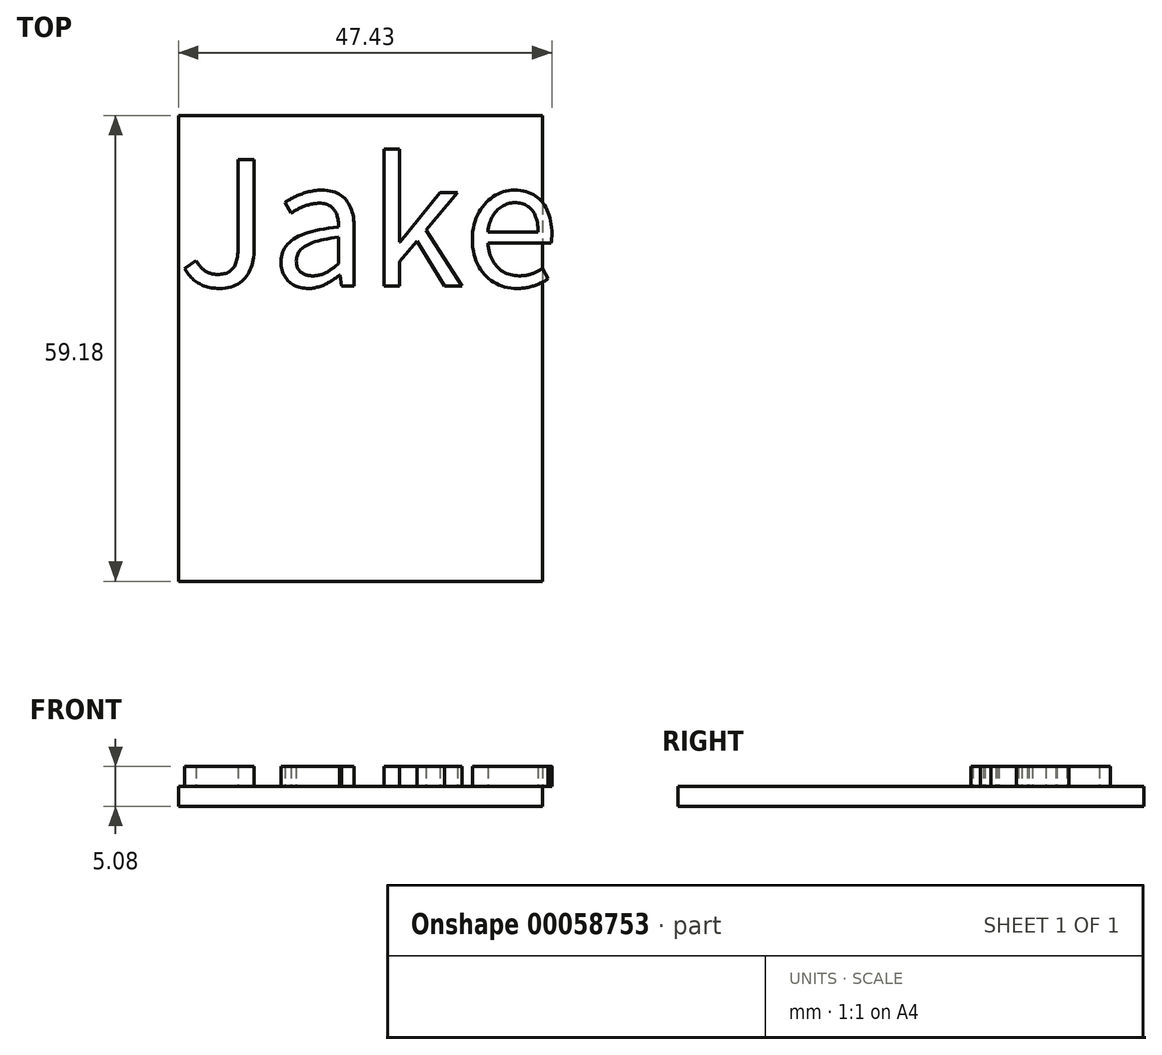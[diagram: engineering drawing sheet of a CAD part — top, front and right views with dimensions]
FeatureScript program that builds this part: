
annotation { "Feature Type Name" : "Feature", "Feature Type Description" : "" }
export const myFeature = defineFeature(function(context is Context, id is Id, definition is map)
    precondition{}
    {
        {
            var Q0;
            Q0=qCreatedBy(makeId("Top.planeOp"),FACE);
            var sketch = newSketch(context, id + "F0", { "sketchPlane" : qUnion([Q0])});
            skLineSegment(sketch, "E0", {"start": v(0, 0) * mm, "end": v(0, 59.18) * mm});
            skLineSegment(sketch, "E1", {"start": v(0, 59.18) * mm, "end": v(46.24, 59.18) * mm});
            skLineSegment(sketch, "E2", {"start": v(46.24, 59.18) * mm, "end": v(46.24, 0) * mm});
            skLineSegment(sketch, "E3", {"start": v(46.24, 0) * mm, "end": v(0, 0) * mm});
            skSolve(sketch);
        }
        {
            var Q0;
            Q0=makeQuery(id+"F0.imprint","IMPRINT",FACE,{"disambiguationData":[TD([[makeQuery(id+"F0.imprint","IMPRINT",EDGE,{"derivedFrom":sQuery(id+"F0.wireOp",EDGE,"E0")}),-1.0]])]});
            extrude(context, id + "F1", {"entities" : qUnion([Q0]), "depth" : 2.54 * mm});
        }
        {
            var Q0;
            Q0=makeQuery(id+"F1.opExtrude","CAP_FACE",FACE,{"disambiguationData":[OSD([sQuery(id+"F0.wireOp",EDGE,"E0"),sQuery(id+"F0.wireOp",EDGE,"E1"),sQuery(id+"F0.wireOp",EDGE,"E2"),sQuery(id+"F0.wireOp",EDGE,"E3")])],"isStart":false});
            var sketch = newSketch(context, id + "F2", { "sketchPlane" : qUnion([Q0])});
            skText(sketch, "E4", { "text": "Jake", "fontName": "NotoSansCJKjp-Regular.otf"});
            const initialGuessF2  = {"E4": [0, 0.0375, 1, 0, 0.01578]};
            skSetInitialGuess(sketch, initialGuessF2);
            skSolve(sketch);
        }
        {
            var Q0;
            Q0 = qSketchRegion(id + "F2", true);
            extrude(context, id + "F3", {"entities" : qUnion([Q0]), "operationType" : NewBodyOperationType.ADD, "depth" : 2.54 * mm});
        }
    });
